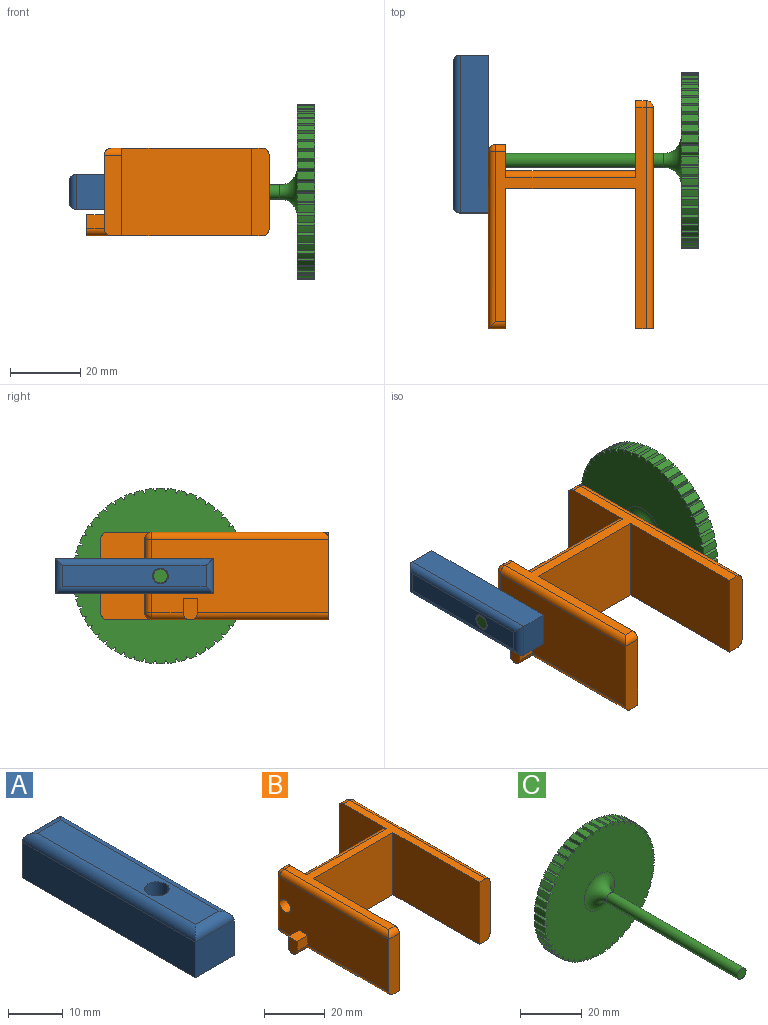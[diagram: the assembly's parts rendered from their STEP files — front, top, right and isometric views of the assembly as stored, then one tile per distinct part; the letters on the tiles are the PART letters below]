
ASSEMBLY  parts=3 mates=2
PART A: 11 faces, bbox 10x45x10 mm
  f0: plane 10x8mm, normal (0,1,0), area 80mm2, adj f1,f2,f4,f7
  f1: plane 45x8mm, normal (-1,0,0), area 360mm2, adj f0,f4,f6,f8
  f2: plane 45x8mm, normal (1,0,0), area 360mm2, adj f0,f4,f6,f9
  f3: plane 41x6mm, normal (0,0,1), area 230.1mm2, adj f5,f7,f8,f9,f10
  f4: plane 45x10mm, normal (0,0,-1), area 434.1mm2, adj f0,f1,f2,f5,f6
  f5: cylinder r=2.25mm len=10mm, axis (0,0,1), area 141.4mm2, adj f3,f4
  f6: plane 10x8mm, normal (0,-1,0), area 80mm2, adj f1,f2,f4,f10
  f7: cylinder r=2mm len=10mm, axis (1,0,0), area 26.8mm2, adj f0,f3,f8,f9
  f8: cylinder r=2mm len=45mm, axis (0,1,0), area 136.8mm2, adj f1,f3,f7,f10
  f9: cylinder r=2mm len=45mm, axis (0,-1,0), area 136.8mm2, adj f2,f3,f7,f10
  f10: cylinder r=2mm len=10mm, axis (-1,0,0), area 26.8mm2, adj f3,f6,f8,f9
PART B: 39 faces, bbox 52x65x25 mm
  f0: plane 50.5x21mm, normal (-1,0,0), area 1024.9mm2, adj f1,f14,f16,f17,f18,f22,f23,f27
  f1: plane 23x5mm, normal (0,-1,0), area 114.1mm2, adj f0,f2,f13,f20,f23
  f2: plane 40x25mm, normal (1,0,0), area 999.1mm2, adj f1,f3,f12,f13,f20
  f3: plane 37x25mm, normal (0,-1,0), area 925mm2, adj f2,f4,f12,f13
  f4: plane 40x25mm, normal (-1,0,0), area 1000mm2, adj f3,f5,f12,f13
  f5: plane 25x5mm, normal (0,-1,0), area 123.3mm2, adj f4,f6,f12,f13,f30,f33
  f6: plane 63x21mm, normal (1,0,0), area 1303.4mm2, adj f5,f15,f30,f33,f36
  f7: plane 21x3mm, normal (0,1,0), area 63mm2, adj f8,f31,f32,f36
  f8: plane 25x22mm, normal (-1,0,0), area 480.4mm2, adj f7,f9,f12,f13,f15,f31,f32,f37
  f9: plane 37x21mm, normal (0,1,0), area 777mm2, adj f8,f10,f37,f38
  f10: plane 25x9.5mm, normal (1,0,0), area 167.9mm2, adj f9,f11,f12,f13,f14,f21,f26,f37
  f11: plane 21x3mm, normal (0,1,0), area 63mm2, adj f10,f21,f26,f27
  f12: plane 63x43mm, normal (0,0,1), area 445.5mm2, adj f2,f3,f4,f5,f8,f10,f20,f21
  f13: plane 63x43mm, normal (0,0,-1), area 451.5mm2, adj f1,f2,f3,f4,f5,f8,f10,f23
  f14: cylinder r=2.5mm len=5mm, axis (1,0,0), area 78.5mm2, adj f0,f10
  f15: cylinder r=2.5mm len=5mm, axis (1,0,0), area 78.5mm2, adj f6,f8
  f16: plane 5x4mm, normal (0,1,0), area 20mm2, adj f0,f18,f19,f25
  f17: plane 5x4mm, normal (0,-1,0), area 20mm2, adj f0,f18,f19,f25
  f18: plane 5x4mm, normal (0,0,1), area 20mm2, adj f0,f16,f17,f19
  f19: plane 6x4mm, normal (-1,0,0), area 22.3mm2, adj f16,f17,f18,f25
  f20: cylinder r=2mm len=5mm, axis (-1,0,0), area 13.4mm2, adj f1,f2,f12,f22
  f21: cylinder r=2mm len=3mm, axis (1,0,0), area 9.4mm2, adj f10,f11,f12,f24
  f22: cylinder r=2mm len=50.5mm, axis (0,1,0), area 156.4mm2, adj f0,f12,f20,f24
  f23: cylinder r=2mm len=39.5mm, axis (0,-1,0), area 120.1mm2, adj f0,f1,f13,f25
  f24: sphere r=2mm, area 6.3mm2, adj f21,f22,f27
  f25: cylinder r=2mm len=7mm, axis (1,0,0), area 36mm2, adj f16,f17,f19,f23,f29
  f26: cylinder r=2mm len=3mm, axis (-1,0,0), area 9.4mm2, adj f10,f11,f13,f28
  f27: cylinder r=2mm len=21mm, axis (0,0,-1), area 66mm2, adj f0,f11,f24,f28
  f28: sphere r=2mm, area 6.3mm2, adj f26,f27,f29
  f29: cylinder r=2mm len=11mm, axis (0,-1,0), area 30.6mm2, adj f0,f13,f25,f28
  f30: cylinder r=2mm len=63mm, axis (0,-1,0), area 197.9mm2, adj f5,f6,f12,f34
  f31: cylinder r=2mm len=3mm, axis (1,0,0), area 9.4mm2, adj f7,f8,f12,f34
  f32: cylinder r=2mm len=3mm, axis (-1,0,0), area 9.4mm2, adj f7,f8,f13,f35
  f33: cylinder r=2mm len=63mm, axis (0,1,0), area 197.9mm2, adj f5,f6,f13,f35
  f34: sphere r=2mm, area 6.3mm2, adj f30,f31,f36
  f35: sphere r=2mm, area 6.3mm2, adj f32,f33,f36
  f36: cylinder r=2mm len=21mm, axis (0,0,1), area 66mm2, adj f6,f7,f34,f35
  f37: cylinder r=2mm len=37mm, axis (-1,0,0), area 116.2mm2, adj f8,f9,f10,f13
  f38: cylinder r=2mm len=37mm, axis (1,0,0), area 116.2mm2, adj f8,f9,f10,f12
PART C: 155 faces, bbox 50x70x50 mm
  f0: cylinder r=2mm len=60mm, axis (0,1,0), area 754mm2, adj f1,f154
  f1: plane 4x4mm, normal (0,-1,0), area 12.6mm2, adj f0
  f2: cylinder r=25mm len=5mm, axis (0,-1,0), area 10.7mm2, adj f3,f151,f152,f153
  f3: plane 5x1mm, normal (-0.89,0,0.45), area 5.6mm2, adj f2,f4,f152,f153
  f4: plane 5x1mm, normal (0.89,0,0.45), area 5.6mm2, adj f3,f5,f152,f153
  f5: cylinder r=25mm len=5mm, axis (0,-1,0), area 10.7mm2, adj f4,f6,f152,f153
  f6: plane 5x1.05mm, normal (-0.94,0,0.33), area 5.6mm2, adj f5,f7,f152,f153
  f7: plane 5x0.92mm, normal (0.83,0,0.56), area 5.6mm2, adj f6,f8,f152,f153
  f8: cylinder r=25mm len=5mm, axis (0,-1,0), area 10.7mm2, adj f7,f9,f152,f153
  f9: plane 5x1.09mm, normal (-0.98,0,0.21), area 5.6mm2, adj f8,f10,f152,f153
  f10: plane 5x0.84mm, normal (0.75,0,0.66), area 5.6mm2, adj f9,f11,f152,f153
  f11: cylinder r=25mm len=5mm, axis (0,-1,0), area 10.7mm2, adj f10,f12,f152,f153
  f12: plane 5x1.11mm, normal (-1,0,0.09), area 5.6mm2, adj f11,f13,f152,f153
  f13: plane 5x0.83mm, normal (0.67,0,0.75), area 5.6mm2, adj f12,f14,f152,f153
  f14: cylinder r=25mm len=5mm, axis (0,-1,0), area 10.7mm2, adj f13,f15,f152,f153
  f15: plane 5x1.11mm, normal (-1,0,-0.04), area 5.6mm2, adj f14,f16,f152,f153
  f16: plane 5x0.92mm, normal (0.57,0,0.82), area 5.6mm2, adj f15,f17,f152,f153
  f17: cylinder r=25mm len=5mm, axis (0,-1,0), area 10.7mm2, adj f16,f18,f152,f153
  f18: plane 5x1.1mm, normal (-0.99,0,-0.16), area 5.6mm2, adj f17,f19,f152,f153
  f19: plane 5x0.99mm, normal (0.46,0,0.89), area 5.6mm2, adj f18,f20,f152,f153
  f20: cylinder r=25mm len=5mm, axis (0,-1,0), area 10.7mm2, adj f19,f21,f152,f153
  f21: plane 5x1.07mm, normal (-0.96,0,-0.28), area 5.6mm2, adj f20,f22,f152,f153
  f22: plane 5x1.05mm, normal (0.34,0,0.94), area 5.6mm2, adj f21,f23,f152,f153
  f23: cylinder r=25mm len=5mm, axis (0,-1,0), area 10.7mm2, adj f22,f24,f152,f153
  f24: plane 5x1.02mm, normal (-0.92,0,-0.4), area 5.6mm2, adj f23,f25,f152,f153
  f25: plane 5x1.09mm, normal (0.22,0,0.97), area 5.6mm2, adj f24,f26,f152,f153
  f26: cylinder r=25mm len=5mm, axis (0,-1,0), area 10.7mm2, adj f25,f27,f152,f153
  f27: plane 5x0.96mm, normal (-0.86,0,-0.51), area 5.6mm2, adj f26,f28,f152,f153
  f28: plane 5x1.11mm, normal (0.1,0,1), area 5.6mm2, adj f27,f29,f152,f153
  f29: cylinder r=25mm len=5mm, axis (0,-1,0), area 10.7mm2, adj f28,f30,f152,f153
  f30: plane 5x0.88mm, normal (-0.79,0,-0.62), area 5.6mm2, adj f29,f31,f152,f153
  f31: plane 5x1.11mm, normal (-0.03,0,1), area 5.6mm2, adj f30,f32,f152,f153
  f32: cylinder r=25mm len=5mm, axis (0,-1,0), area 10.7mm2, adj f31,f33,f152,f153
  f33: plane 5x0.79mm, normal (-0.7,0,-0.71), area 5.6mm2, adj f32,f34,f152,f153
  f34: plane 5x1.1mm, normal (-0.15,0,0.99), area 5.6mm2, adj f33,f35,f152,f153
  f35: cylinder r=25mm len=5mm, axis (0,-1,0), area 10.7mm2, adj f34,f36,f152,f153
  f36: plane 5x0.88mm, normal (-0.61,0,-0.79), area 5.6mm2, adj f35,f37,f152,f153
  f37: plane 5x1.07mm, normal (-0.27,0,0.96), area 5.6mm2, adj f36,f38,f152,f153
  f38: cylinder r=25mm len=5mm, axis (0,-1,0), area 10.7mm2, adj f37,f39,f152,f153
  f39: plane 5x0.96mm, normal (-0.5,0,-0.86), area 5.6mm2, adj f38,f40,f152,f153
  f40: plane 5x1.02mm, normal (-0.39,0,0.92), area 5.6mm2, adj f39,f41,f152,f153
  f41: cylinder r=25mm len=5mm, axis (0,-1,0), area 10.7mm2, adj f40,f42,f152,f153
  f42: plane 5x1.02mm, normal (-0.39,0,-0.92), area 5.6mm2, adj f41,f43,f152,f153
  f43: plane 5x0.96mm, normal (-0.5,0,0.86), area 5.6mm2, adj f42,f44,f152,f153
  f44: cylinder r=25mm len=5mm, axis (0,-1,0), area 10.7mm2, adj f43,f45,f152,f153
  f45: plane 5x1.07mm, normal (-0.27,0,-0.96), area 5.6mm2, adj f44,f46,f152,f153
  f46: plane 5x0.88mm, normal (-0.61,0,0.79), area 5.6mm2, adj f45,f47,f152,f153
  f47: cylinder r=25mm len=5mm, axis (0,-1,0), area 10.7mm2, adj f46,f48,f152,f153
  f48: plane 5x1.1mm, normal (-0.15,0,-0.99), area 5.6mm2, adj f47,f49,f152,f153
  f49: plane 5x0.79mm, normal (-0.7,0,0.71), area 5.6mm2, adj f48,f50,f152,f153
  f50: cylinder r=25mm len=5mm, axis (0,-1,0), area 10.7mm2, adj f49,f51,f152,f153
  f51: plane 5x1.11mm, normal (-0.03,0,-1), area 5.6mm2, adj f50,f52,f152,f153
  f52: plane 5x0.88mm, normal (-0.79,0,0.62), area 5.6mm2, adj f51,f53,f152,f153
  f53: cylinder r=25mm len=5mm, axis (0,-1,0), area 10.7mm2, adj f52,f54,f152,f153
  f54: plane 5x1.11mm, normal (0.1,0,-1), area 5.6mm2, adj f53,f55,f152,f153
  f55: plane 5x0.96mm, normal (-0.86,0,0.51), area 5.6mm2, adj f54,f56,f152,f153
  f56: cylinder r=25mm len=5mm, axis (0,-1,0), area 10.7mm2, adj f55,f57,f152,f153
  f57: plane 5x1.09mm, normal (0.22,0,-0.97), area 5.6mm2, adj f56,f58,f152,f153
  f58: plane 5x1.02mm, normal (-0.92,0,0.4), area 5.6mm2, adj f57,f59,f152,f153
  f59: cylinder r=25mm len=5mm, axis (0,-1,0), area 10.7mm2, adj f58,f60,f152,f153
  f60: plane 5x1.05mm, normal (0.34,0,-0.94), area 5.6mm2, adj f59,f61,f152,f153
  f61: plane 5x1.07mm, normal (-0.96,0,0.28), area 5.6mm2, adj f60,f62,f152,f153
  f62: cylinder r=25mm len=5mm, axis (0,-1,0), area 10.7mm2, adj f61,f63,f152,f153
  f63: plane 5x0.99mm, normal (0.46,0,-0.89), area 5.6mm2, adj f62,f64,f152,f153
  f64: plane 5x1.1mm, normal (-0.99,0,0.16), area 5.6mm2, adj f63,f65,f152,f153
  f65: cylinder r=25mm len=5mm, axis (0,-1,0), area 10.7mm2, adj f64,f66,f152,f153
  f66: plane 5x0.92mm, normal (0.57,0,-0.82), area 5.6mm2, adj f65,f67,f152,f153
  f67: plane 5x1.11mm, normal (-1,0,0.04), area 5.6mm2, adj f66,f68,f152,f153
  f68: cylinder r=25mm len=5mm, axis (0,-1,0), area 10.7mm2, adj f67,f69,f152,f153
  f69: plane 5x0.83mm, normal (0.67,0,-0.75), area 5.6mm2, adj f68,f70,f152,f153
  f70: plane 5x1.11mm, normal (-1,0,-0.09), area 5.6mm2, adj f69,f71,f152,f153
  f71: cylinder r=25mm len=5mm, axis (0,-1,0), area 10.7mm2, adj f70,f72,f152,f153
  f72: plane 5x0.84mm, normal (0.75,0,-0.66), area 5.6mm2, adj f71,f73,f152,f153
  f73: plane 5x1.09mm, normal (-0.98,0,-0.21), area 5.6mm2, adj f72,f74,f152,f153
  f74: cylinder r=25mm len=5mm, axis (0,-1,0), area 10.7mm2, adj f73,f75,f152,f153
  f75: plane 5x0.92mm, normal (0.83,0,-0.56), area 5.6mm2, adj f74,f76,f152,f153
  f76: plane 5x1.05mm, normal (-0.94,0,-0.33), area 5.6mm2, adj f75,f77,f152,f153
  f77: cylinder r=25mm len=5mm, axis (0,-1,0), area 10.7mm2, adj f76,f78,f152,f153
  f78: plane 5x1mm, normal (0.89,0,-0.45), area 5.6mm2, adj f77,f79,f152,f153
  f79: plane 5x1mm, normal (-0.89,0,-0.45), area 5.6mm2, adj f78,f80,f152,f153
  f80: cylinder r=25mm len=5mm, axis (0,-1,0), area 10.7mm2, adj f79,f81,f152,f153
  f81: plane 5x1.05mm, normal (0.94,0,-0.33), area 5.6mm2, adj f80,f82,f152,f153
  f82: plane 5x0.92mm, normal (-0.83,0,-0.56), area 5.6mm2, adj f81,f83,f152,f153
  f83: cylinder r=25mm len=5mm, axis (0,-1,0), area 10.7mm2, adj f82,f84,f152,f153
  f84: plane 5x1.09mm, normal (0.98,0,-0.21), area 5.6mm2, adj f83,f85,f152,f153
  f85: plane 5x0.84mm, normal (-0.75,0,-0.66), area 5.6mm2, adj f84,f86,f152,f153
  f86: cylinder r=25mm len=5mm, axis (0,-1,0), area 10.7mm2, adj f85,f87,f152,f153
  f87: plane 5x1.11mm, normal (1,0,-0.09), area 5.6mm2, adj f86,f88,f152,f153
  f88: plane 5x0.83mm, normal (-0.67,0,-0.75), area 5.6mm2, adj f87,f89,f152,f153
  f89: cylinder r=25mm len=5mm, axis (0,-1,0), area 10.7mm2, adj f88,f90,f152,f153
  f90: plane 5x1.11mm, normal (1,0,0.04), area 5.6mm2, adj f89,f91,f152,f153
  f91: plane 5x0.92mm, normal (-0.57,0,-0.82), area 5.6mm2, adj f90,f92,f152,f153
  f92: cylinder r=25mm len=5mm, axis (0,-1,0), area 10.7mm2, adj f91,f93,f152,f153
  f93: plane 5x1.1mm, normal (0.99,0,0.16), area 5.6mm2, adj f92,f94,f152,f153
  f94: plane 5x0.99mm, normal (-0.46,0,-0.89), area 5.6mm2, adj f93,f95,f152,f153
  f95: cylinder r=25mm len=5mm, axis (0,-1,0), area 10.7mm2, adj f94,f96,f152,f153
  f96: plane 5x1.07mm, normal (0.96,0,0.28), area 5.6mm2, adj f95,f97,f152,f153
  f97: plane 5x1.05mm, normal (-0.34,0,-0.94), area 5.6mm2, adj f96,f98,f152,f153
  f98: cylinder r=25mm len=5mm, axis (0,-1,0), area 10.7mm2, adj f97,f99,f152,f153
  f99: plane 5x1.02mm, normal (0.92,0,0.4), area 5.6mm2, adj f98,f100,f152,f153
  f100: plane 5x1.09mm, normal (-0.22,0,-0.97), area 5.6mm2, adj f99,f101,f152,f153
  f101: cylinder r=25mm len=5mm, axis (0,-1,0), area 10.7mm2, adj f100,f102,f152,f153
  f102: plane 5x0.96mm, normal (0.86,0,0.51), area 5.6mm2, adj f101,f103,f152,f153
  f103: plane 5x1.11mm, normal (-0.1,0,-1), area 5.6mm2, adj f102,f104,f152,f153
  f104: cylinder r=25mm len=5mm, axis (0,-1,0), area 10.7mm2, adj f103,f105,f152,f153
  f105: plane 5x0.88mm, normal (0.79,0,0.62), area 5.6mm2, adj f104,f106,f152,f153
  f106: plane 5x1.11mm, normal (0.03,0,-1), area 5.6mm2, adj f105,f107,f152,f153
  f107: cylinder r=25mm len=5mm, axis (0,-1,0), area 10.7mm2, adj f106,f108,f152,f153
  f108: plane 5x0.79mm, normal (0.7,0,0.71), area 5.6mm2, adj f107,f109,f152,f153
  f109: plane 5x1.1mm, normal (0.15,0,-0.99), area 5.6mm2, adj f108,f110,f152,f153
  f110: cylinder r=25mm len=5mm, axis (0,-1,0), area 10.7mm2, adj f109,f111,f152,f153
  f111: plane 5x0.88mm, normal (0.61,0,0.79), area 5.6mm2, adj f110,f112,f152,f153
  f112: plane 5x1.07mm, normal (0.27,0,-0.96), area 5.6mm2, adj f111,f113,f152,f153
  f113: cylinder r=25mm len=5mm, axis (0,-1,0), area 10.7mm2, adj f112,f114,f152,f153
  f114: plane 5x0.96mm, normal (0.5,0,0.86), area 5.6mm2, adj f113,f115,f152,f153
  f115: plane 5x1.02mm, normal (0.39,0,-0.92), area 5.6mm2, adj f114,f116,f152,f153
  f116: cylinder r=25mm len=5mm, axis (0,-1,0), area 10.7mm2, adj f115,f117,f152,f153
  f117: plane 5x1.02mm, normal (0.39,0,0.92), area 5.6mm2, adj f116,f118,f152,f153
  f118: plane 5x0.96mm, normal (0.5,0,-0.86), area 5.6mm2, adj f117,f119,f152,f153
  f119: cylinder r=25mm len=5mm, axis (0,-1,0), area 10.7mm2, adj f118,f120,f152,f153
  f120: plane 5x1.07mm, normal (0.27,0,0.96), area 5.6mm2, adj f119,f121,f152,f153
  f121: plane 5x0.88mm, normal (0.61,0,-0.79), area 5.6mm2, adj f120,f122,f152,f153
  f122: cylinder r=25mm len=5mm, axis (0,-1,0), area 10.7mm2, adj f121,f123,f152,f153
  f123: plane 5x1.1mm, normal (0.15,0,0.99), area 5.6mm2, adj f122,f124,f152,f153
  f124: plane 5x0.79mm, normal (0.7,0,-0.71), area 5.6mm2, adj f123,f125,f152,f153
  f125: cylinder r=25mm len=5mm, axis (0,-1,0), area 10.7mm2, adj f124,f126,f152,f153
  f126: plane 5x1.11mm, normal (0.03,0,1), area 5.6mm2, adj f125,f127,f152,f153
  f127: plane 5x0.88mm, normal (0.79,0,-0.62), area 5.6mm2, adj f126,f128,f152,f153
  f128: cylinder r=25mm len=5mm, axis (0,-1,0), area 10.7mm2, adj f127,f129,f152,f153
  f129: plane 5x1.11mm, normal (-0.1,0,1), area 5.6mm2, adj f128,f130,f152,f153
  f130: plane 5x0.96mm, normal (0.86,0,-0.51), area 5.6mm2, adj f129,f131,f152,f153
  f131: cylinder r=25mm len=5mm, axis (0,-1,0), area 10.7mm2, adj f130,f132,f152,f153
  f132: plane 5x1.09mm, normal (-0.22,0,0.97), area 5.6mm2, adj f131,f133,f152,f153
  f133: plane 5x1.02mm, normal (0.92,0,-0.4), area 5.6mm2, adj f132,f134,f152,f153
  f134: cylinder r=25mm len=5mm, axis (0,-1,0), area 10.7mm2, adj f133,f135,f152,f153
  f135: plane 5x1.05mm, normal (-0.34,0,0.94), area 5.6mm2, adj f134,f136,f152,f153
  f136: plane 5x1.07mm, normal (0.96,0,-0.28), area 5.6mm2, adj f135,f137,f152,f153
  f137: cylinder r=25mm len=5mm, axis (0,-1,0), area 10.7mm2, adj f136,f138,f152,f153
  f138: plane 5x0.99mm, normal (-0.46,0,0.89), area 5.6mm2, adj f137,f139,f152,f153
  f139: plane 5x1.1mm, normal (0.99,0,-0.16), area 5.6mm2, adj f138,f140,f152,f153
  f140: cylinder r=25mm len=5mm, axis (0,-1,0), area 10.7mm2, adj f139,f141,f152,f153
  f141: plane 5x0.92mm, normal (-0.57,0,0.82), area 5.6mm2, adj f140,f142,f152,f153
  f142: plane 5x1.11mm, normal (1,0,-0.04), area 5.6mm2, adj f141,f143,f152,f153
  f143: cylinder r=25mm len=5mm, axis (0,-1,0), area 10.7mm2, adj f142,f144,f152,f153
  f144: plane 5x0.83mm, normal (-0.67,0,0.75), area 5.6mm2, adj f143,f145,f152,f153
  f145: plane 5x1.11mm, normal (1,0,0.09), area 5.6mm2, adj f144,f146,f152,f153
  f146: cylinder r=25mm len=5mm, axis (0,-1,0), area 10.7mm2, adj f145,f147,f152,f153
  f147: plane 5x0.84mm, normal (-0.75,0,0.66), area 5.6mm2, adj f146,f148,f152,f153
  f148: plane 5x1.09mm, normal (0.98,0,0.21), area 5.6mm2, adj f147,f149,f152,f153
  f149: cylinder r=25mm len=5mm, axis (0,-1,0), area 10.7mm2, adj f148,f150,f152,f153
  f150: plane 5x0.92mm, normal (-0.83,0,0.56), area 5.6mm2, adj f149,f151,f152,f153
  f151: plane 5x1.05mm, normal (0.94,0,0.33), area 5.6mm2, adj f2,f150,f152,f153
  f152: plane 50x49.99mm, normal (0,1,0), area 1938.5mm2, adj f2,f3,f4,f5,f6,f7,f8,f9
  f153: plane 50x49.99mm, normal (0,-1,0), area 1784.5mm2, adj f2,f3,f4,f5,f6,f7,f8,f9
  f154: torus R=7mm, axis (0,-1,0), area 188.4mm2, adj f0,f153
PLACE A rot(axis=(0,-1,0),90deg) t=(0.57,17.95,2.12)mm
PLACE B t=(0.57,4.95,-10.38)mm
PLACE C rot(axis=(-0.58,-0.58,-0.58),120deg) t=(55.57,7.95,2.12)mm
MATE planar C.f0 <-> B.f14  axis (-1,0,0) through (-9.43,7.95,2.12)mm
MATE planar A.f5 <-> C.f0  axis (-1,0,0) through (-9.43,7.95,2.12)mm
